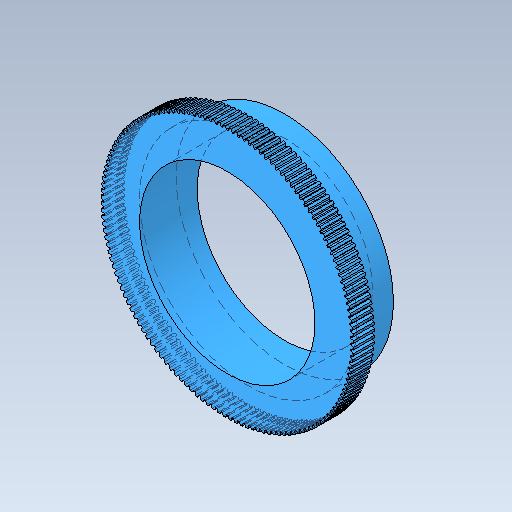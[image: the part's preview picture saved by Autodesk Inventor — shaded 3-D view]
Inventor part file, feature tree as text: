
AUTODESK INVENTOR PART (.ipt)
format: ipt  version: 2020 (Build 240168000, 168)  size: 1,049,088 bytes
history: native  units: mm
features: extrude x4, sketch x4, other x1
ambient origin geometry x8: Origin, YZ Plane, XZ Plane, XY Plane, X Axis, Y Axis, Z Axis, Center Point
bodies: Body1 (feature_tree)
feature tree (9):
  other  "ソリッド1"
  extrude  "押し出し1"  Depth=15.5mm
  extrude  "押し出し2"  Depth=2.6mm TaperAngle=0.0deg
  extrude  "押し出し3"  Depth=18.0mm
  extrude  "押し出し4"  Depth=1.5mm TaperAngle=0.0deg
  sketch  "スケッチ1"
  sketch  "スケッチ2"
  sketch  "スケッチ3"
  sketch  "スケッチ4"
